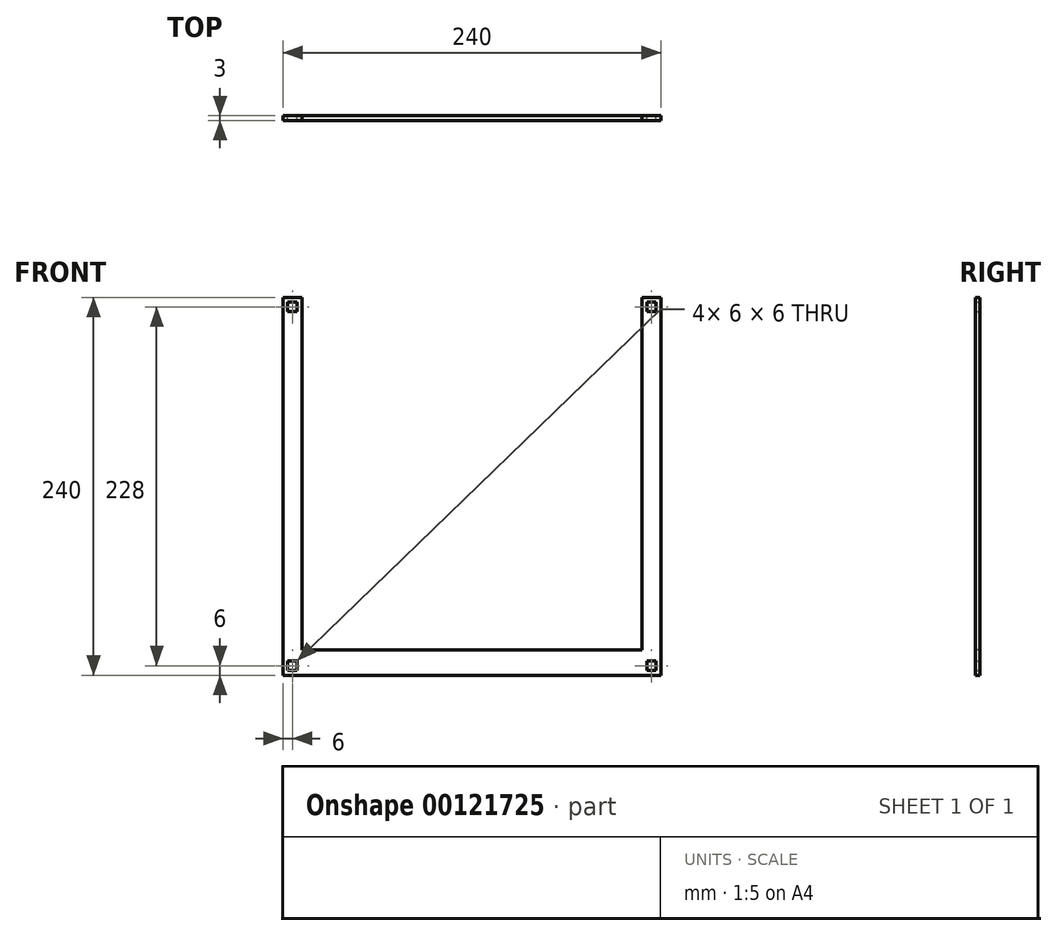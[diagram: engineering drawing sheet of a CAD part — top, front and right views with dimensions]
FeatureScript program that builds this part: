
annotation { "Feature Type Name" : "Feature", "Feature Type Description" : "" }
export const myFeature = defineFeature(function(context is Context, id is Id, definition is map)
    precondition{}
    {
        {
            assignVariable(context, id + "F0", {"name" : "thicknessWood", "anyValue" : 3});
        }
        {
            var Q0;
            Q0=qCreatedBy(makeId("Front.planeOp"),FACE);
            var sketch = newSketch(context, id + "F1", { "sketchPlane" : qUnion([Q0])});
            skLineSegment(sketch, "E0.bottom", {"start": v(0, 0) * mm, "end": v(240, 0) * mm});
            skLineSegment(sketch, "E0.top", {"start": v(0, 240) * mm, "end": v(240, 240) * mm});
            skLineSegment(sketch, "E0.left", {"start": v(0, 0) * mm, "end": v(0, 240) * mm});
            skLineSegment(sketch, "E0.right", {"start": v(240, 0) * mm, "end": v(240, 240) * mm});
            skLineSegment(sketch, "E1.bottom", {"start": v(16, 224) * mm, "end": v(224, 224) * mm});
            skLineSegment(sketch, "E1.top", {"start": v(16, 16) * mm, "end": v(224, 16) * mm});
            skLineSegment(sketch, "E1.left", {"start": v(16, 224) * mm, "end": v(16, 16) * mm});
            skLineSegment(sketch, "E1.right", {"start": v(224, 224) * mm, "end": v(224, 16) * mm});
            skLineSegment(sketch, "E2.bottom", {"start": v(9, 237) * mm, "end": v(3, 237) * mm});
            skLineSegment(sketch, "E2.top", {"start": v(9, 231) * mm, "end": v(3, 231) * mm});
            skLineSegment(sketch, "E2.left", {"start": v(9, 237) * mm, "end": v(9, 231) * mm});
            skLineSegment(sketch, "E2.right", {"start": v(3, 237) * mm, "end": v(3, 231) * mm});
            skLineSegment(sketch, "E3", {"start": v(120, 240) * mm, "end": v(120, 0) * mm, "construction": true});
            skLineSegment(sketch, "E4", {"start": v(0, 120) * mm, "end": v(240, 120) * mm, "construction": true});
            skSolve(sketch);
        }
        {
            var Q0;
            Q0=makeQuery(id+"F1.imprint","IMPRINT",FACE,{"disambiguationData":[TD([[makeQuery(id+"F1.imprint","IMPRINT",EDGE,{"derivedFrom":sQuery(id+"F1.wireOp",EDGE,"E0.bottom")}),1.0]])]});
            var Q1;
            Q1=makeQuery(id+"F1.imprint","IMPRINT",FACE,{"disambiguationData":[TD([[makeQuery(id+"F1.imprint","IMPRINT",EDGE,{"derivedFrom":sQuery(id+"F1.wireOp",EDGE,"E2.bottom")}),1.0]])]});
            var Q2;
            Q2=sQuery(id+"F1.wireOp",EDGE,"E1.left");
            extrude(context, id + "F2", {"entities" : qUnion([Q0, Q1]), "surfaceEntities" : qUnion([Q2]), "depth" : (getVariable(context, 'thicknessWood')) * mm});
        }
        {
            var Q0;
            Q0=makeQuery(id+"F1.imprint","IMPRINT",FACE,{"disambiguationData":[TD([[makeQuery(id+"F1.imprint","IMPRINT",EDGE,{"derivedFrom":sQuery(id+"F1.wireOp",EDGE,"E2.bottom")}),1.0]])]});
            extrude(context, id + "F3", {"entities" : qUnion([Q0]), "operationType" : NewBodyOperationType.REMOVE, "depth" : 25 * mm});
        }
        {
            var Q0;
            Q0=makeQuery(id+"F2.opExtrude","SWEPT_FACE",FACE,{"disambiguationData":[OSD([sQuery(id+"F1.wireOp",EDGE,"E0.left")])]});
            var Q1;
            Q1=makeQuery(id+"F2.opExtrude","SWEPT_FACE",FACE,{"disambiguationData":[OSD([sQuery(id+"F1.wireOp",EDGE,"E0.right")])]});
            cPlane(context, id + "F4", {"entities" : qUnion([Q0, Q1]), "cplaneType" : CPlaneType.MID_PLANE, "offset" : 25 * mm, "width" : 150 * mm, "height" : 150 * mm});
        }
        {
            var Q0;
            Q0=makeQuery(id+"F2.opExtrude","SWEPT_BODY",BODY,{"disambiguationData":[OSD([sQuery(id+"F1.wireOp",EDGE,"E0.bottom"),sQuery(id+"F1.wireOp",EDGE,"E0.top"),sQuery(id+"F1.wireOp",EDGE,"E0.left"),sQuery(id+"F1.wireOp",EDGE,"E0.right"),sQuery(id+"F1.wireOp",EDGE,"E1.bottom"),sQuery(id+"F1.wireOp",EDGE,"E1.top"),sQuery(id+"F1.wireOp",EDGE,"E1.left"),sQuery(id+"F1.wireOp",EDGE,"E1.right")])]});
            var Q1;
            Q1=qCreatedBy(id+"F4.planeOp",FACE);
            mirror(context, id + "F5", {"operationType" : NewBodyOperationType.INTERSECT, "entities" : qUnion([Q0]), "mirrorPlane" : qUnion([Q1])});
        }
        {
            var Q0;
            Q0=makeQuery(id+"F2.opExtrude","SWEPT_FACE",FACE,{"disambiguationData":[OSD([sQuery(id+"F1.wireOp",EDGE,"E0.top")])]});
            var Q1;
            Q1=makeQuery(id+"F2.opExtrude","SWEPT_FACE",FACE,{"disambiguationData":[OSD([sQuery(id+"F1.wireOp",EDGE,"E0.bottom")])]});
            cPlane(context, id + "F6", {"entities" : qUnion([Q0, Q1]), "cplaneType" : CPlaneType.MID_PLANE, "offset" : 25 * mm, "width" : 150 * mm, "height" : 150 * mm});
        }
        {
            var Q0;
            Q0=makeQuery(id+"F2.opExtrude","SWEPT_BODY",BODY,{"disambiguationData":[OSD([sQuery(id+"F1.wireOp",EDGE,"E0.bottom"),sQuery(id+"F1.wireOp",EDGE,"E0.top"),sQuery(id+"F1.wireOp",EDGE,"E0.left"),sQuery(id+"F1.wireOp",EDGE,"E0.right"),sQuery(id+"F1.wireOp",EDGE,"E1.bottom"),sQuery(id+"F1.wireOp",EDGE,"E1.top"),sQuery(id+"F1.wireOp",EDGE,"E1.left"),sQuery(id+"F1.wireOp",EDGE,"E1.right")])]});
            var Q1;
            Q1=qCreatedBy(id+"F6.planeOp",FACE);
            mirror(context, id + "F7", {"operationType" : NewBodyOperationType.INTERSECT, "entities" : qUnion([Q0]), "mirrorPlane" : qUnion([Q1])});
        }
        {
            var Q0;
            Q0=makeQuery(id+"F2.opExtrude","CAP_FACE",FACE,{"disambiguationData":[OSD([sQuery(id+"F1.wireOp",EDGE,"E0.bottom"),sQuery(id+"F1.wireOp",EDGE,"E0.top"),sQuery(id+"F1.wireOp",EDGE,"E0.left"),sQuery(id+"F1.wireOp",EDGE,"E0.right"),sQuery(id+"F1.wireOp",EDGE,"E1.bottom"),sQuery(id+"F1.wireOp",EDGE,"E1.top"),sQuery(id+"F1.wireOp",EDGE,"E1.left"),sQuery(id+"F1.wireOp",EDGE,"E1.right")])],"isStart":false});
            var sketch = newSketch(context, id + "F8", { "sketchPlane" : qUnion([Q0])});
            skLineSegment(sketch, "E5.bottom", {"start": v(12, 256) * mm, "end": v(228, 256) * mm});
            skLineSegment(sketch, "E5.top", {"start": v(12, 16) * mm, "end": v(228, 16) * mm});
            skLineSegment(sketch, "E5.left", {"start": v(12, 256) * mm, "end": v(12, 16) * mm});
            skLineSegment(sketch, "E5.right", {"start": v(228, 256) * mm, "end": v(228, 16) * mm});
            skSolve(sketch);
        }
        {
            var Q0;
            {var subQ0=sQuery(id+"F8.wireOp",EDGE,"E5.bottom");Q0=makeQuery(id+"F8.imprint","IMPRINT",FACE,{"disambiguationData":[TD([[makeQuery(id+"F8.imprint","IMPRINT",EDGE,{"derivedFrom":subQ0}),-1.0]])]});}
            var Q1;
            Q1=makeQuery(id+"F8.imprint","IMPRINT",FACE,{"disambiguationData":[TD([[makeQuery(id+"F8.imprint","IMPRINT",EDGE,{"derivedFrom":makeQuery(id+"F2.opExtrude","CAP_EDGE",EDGE,{"disambiguationData":[OSD([sQuery(id+"F1.wireOp",EDGE,"E1.bottom")])],"isStart":false})}),-1.0]])]});
            var Q2;
            Q2=makeQuery(id+"F8.imprint","IMPRINT",FACE,{"disambiguationData":[TD([[makeQuery(id+"F8.imprint","IMPRINT",EDGE,{"derivedFrom":makeQuery(id+"F2.opExtrude","CAP_EDGE",EDGE,{"disambiguationData":[OSD([sQuery(id+"F1.wireOp",EDGE,"E1.bottom")])],"isStart":false})}),1.0]])]});
            extrude(context, id + "F9", {"entities" : qUnion([Q0, Q1, Q2]), "operationType" : NewBodyOperationType.REMOVE, "endBound" : BoundingType.THROUGH_ALL, "oppositeDirection" : true, "depth" : 25 * mm});
        }
    });
